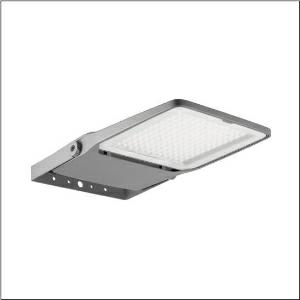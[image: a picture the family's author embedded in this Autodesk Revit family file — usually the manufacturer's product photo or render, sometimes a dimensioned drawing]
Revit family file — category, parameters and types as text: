
# Revit family: floodlight_fl_20_midi___pl61_5xa7682e1c2ac_7ec6
name_source: partatom
category: Lighting Fixtures
units: mm (PartAtom-declared; Revit-internal decimal feet)

## family parameters
Cut with Voids When Loaded = No
Host = Face
Light Source = No
Part Type = Normal
Room Calculation Point = No
Round Connector Dimension = Use Diameter
Shared = No

## types (1)
- --- (1 x LED 3000K / CRI = 80 (unbekannt), 21280 lm, 3000K)
    Apparent Load = 208 VA
    CIE Flux Codes = 33 65 98 100 100
    Color Rendering = 80
    Color Temperature = 3000K
    Default Elevation = 1800 mm
    Description = Floodlight FL 20 midi, floodlight, primary light control with lens, of plastic, primary optical cover: protective disc, of toughened safety glass, transparent, light distribution: PL61, light emission: direct distribution, primary light characteristic: asymmetric, installation type: surface-mounted, LED High Power LED, rated luminous flux: 21.280 lm, light colour: 830, colour temperature: 3000K, control gear: ECG Plus, control: digital communication interface, time-dependent luminous flux control, flexible luminous flux parameterisation, power reduction, overheat protection, electronic power reduction, with terminal, 5-pole, max. 2.5mm², mains connection: 220..240V, AC, 50/60Hz, rated input power: 208W, LED unit, of diecast aluminium, powder-coated, Siteco® metallic grey (DB 702S), length: 731 mm, width: 450 mm, height: 76mm, housing frame, of diecast aluminium, powder-coated, Siteco® metallic grey (DB 702S), wall fastening, of steel, powder-coated, Siteco® metallic grey (DB 702S), DALIprotection rating (complete): IP66, insulation class (complete): insulation class II (safety insulation), certification: CE, ENEC, VDE, protection symbol: D, permissible ambient temperature for indoor applications: -40..+40°C, permissible ambient temperature for outdoor applications: -40..+50°C, standard: DIN EN 12944, packaging unit: 1 piece

Light Distribution: PL61
    Height = 76 mm
    Lamp = 1 x LED 3000K / CRI >= 80 (unbekannt)
    Lamp Light Flux = 21280 lm
    Lamp count = 1
    Length = 731 mm
    Luminous efficacy = 102 lm/W
    Manufacturer = Siteco
    ModVariant = No
    Model = 5XA7682E1C2AC
    Number of Poles = 1
    OnlyDefault = Yes
    Power Factor = 1
    Product Name = Floodlight FL 20 midi | PL61
    Product group = floodlight | pylon top
    ProductGroupID = 6101
    Protection Class = Protection class II
    Protection Degree = IP 66
    RLX_Detail_Level = 1
    RlxData = <blob elided: 91913 chars, md5=e52592f3>
    Socket = socket
    Standby Power = 0 W
    System Light Flux = 21280 lm
    System Power = 208 W
    Type Comments = factory setting: luminous flux: 100 % | dim-lin: 254 | 484 mA
    Type Image = l_1005944.jpg
    URL = http://relux.com
    VarID = @adj_142391
    Voltage = 0 V
    Weight = 0.00 kg
    Width = 450 mm

## geometry (parser evidence)
native form markers: Blend x4, Sweep x13
no freeform markers — native parametric forms only
